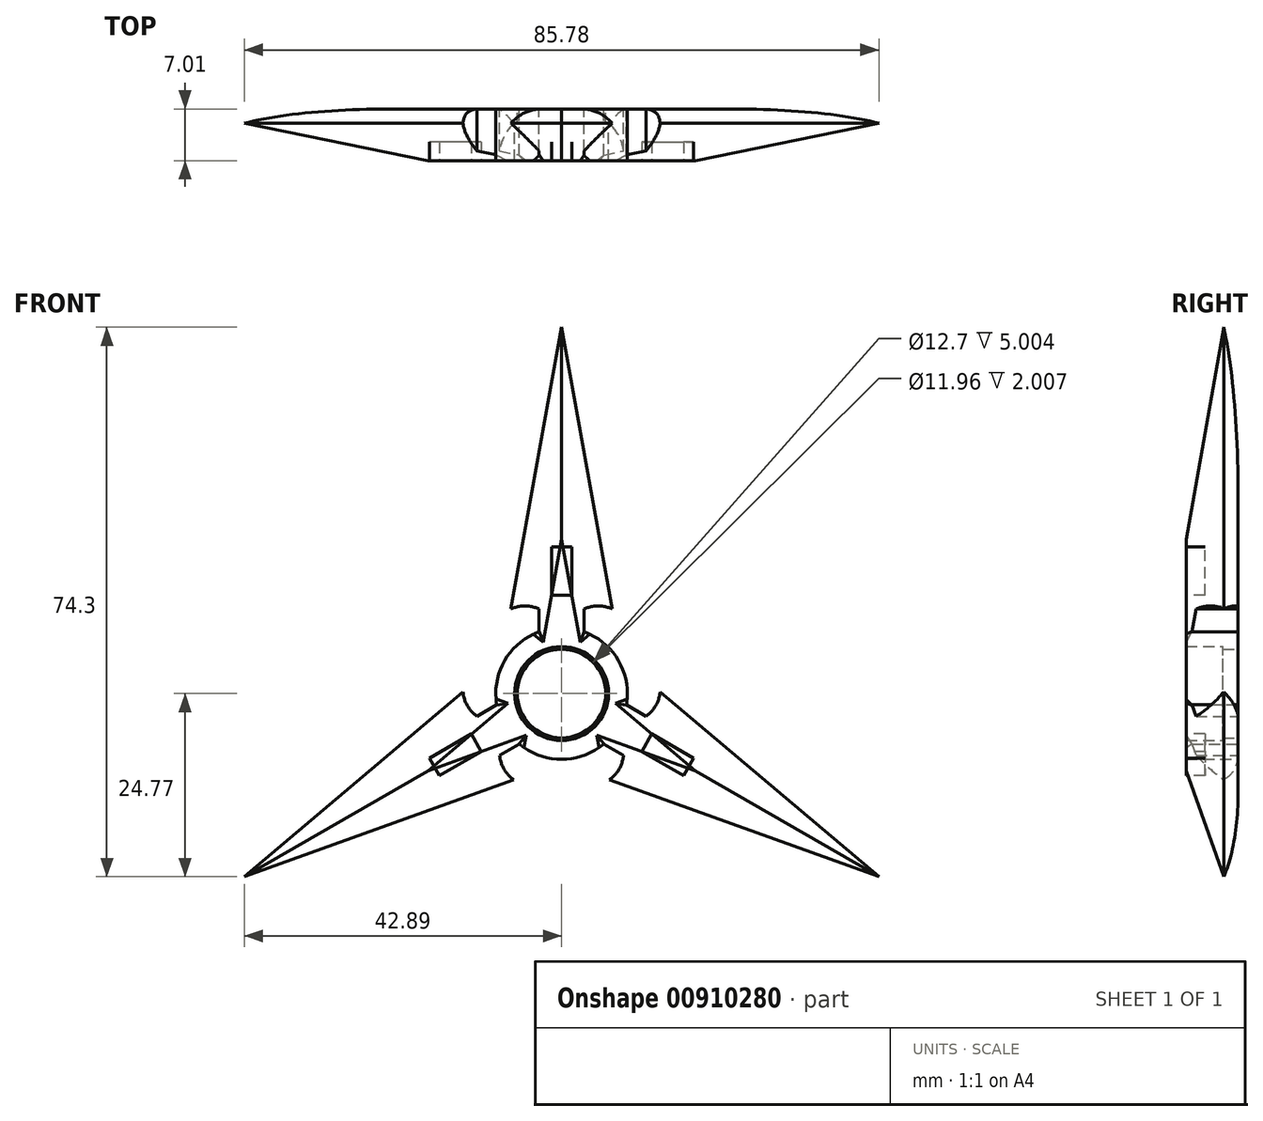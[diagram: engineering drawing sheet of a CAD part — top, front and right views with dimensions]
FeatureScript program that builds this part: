
annotation { "Feature Type Name" : "Feature", "Feature Type Description" : "" }
export const myFeature = defineFeature(function(context is Context, id is Id, definition is map)
    precondition{}
    {
        {
            var Q0;
            Q0=qCreatedBy(makeId("Front.planeOp"),FACE);
            var sketch = newSketch(context, id + "F0", { "sketchPlane" : qUnion([Q0])});
            skCircle(sketch, "E0", {"center": v(0, 0) * mm, "radius": 8.9 * mm});
            skCircle(sketch, "E1", {"center": v(0, 0) * mm, "radius": 6.35 * mm});
            skPoint(sketch, "E2", {"position": v(0, 8.9) * mm});
            skPoint(sketch, "E3", {"position": v(-3.05, 8.89) * mm});
            skPoint(sketch, "E4", {"position": v(3.05, 8.9) * mm});
            skLineSegment(sketch, "E5", {"start": v(-3.05, 8.89) * mm, "end": v(-3.05, 8.35) * mm});
            skLineSegment(sketch, "E6", {"start": v(3.05, 8.9) * mm, "end": v(3.05, 8.35) * mm});
            skLineSegment(sketch, "E7", {"start": v(3.05, 8.9) * mm, "end": v(3.05, 11.43) * mm});
            skLineSegment(sketch, "E8", {"start": v(-3.05, 8.89) * mm, "end": v(-3.05, 11.43) * mm});
            skPoint(sketch, "E9", {"position": v(-6.86, 11.43) * mm});
            skPoint(sketch, "E10", {"position": v(6.86, 11.43) * mm});
            skArc(sketch, "E11", {"start": v(-3.05, 11.43) * mm, "mid": v(-4.95, 11.84) * mm, "end": v(-6.86, 11.43) * mm});
            skArc(sketch, "E12", {"start": v(6.86, 11.43) * mm, "mid": v(4.95, 11.84) * mm, "end": v(3.05, 11.43) * mm});
            skPoint(sketch, "E13", {"position": v(6.86, 10.93) * mm});
            skPoint(sketch, "E14", {"position": v(-6.86, 10.75) * mm});
            skPoint(sketch, "E15", {"position": v(0, 49.53) * mm});
            skLineSegment(sketch, "E16", {"start": v(-6.86, 11.43) * mm, "end": v(0, 49.53) * mm});
            skLineSegment(sketch, "E17", {"start": v(0, 49.53) * mm, "end": v(6.86, 11.43) * mm});
            skSolve(sketch);
        }
        {
            var Q0;
            {var subQ1=sQuery(id+"F0.wireOp",EDGE,"E5");Q0=makeQuery(id+"F0.imprint","IMPRINT",FACE,{"disambiguationData":[TD([[makeQuery(id+"F0.imprint","IMPRINT",EDGE,{"derivedFrom":subQ1}),1.0]])]});}
            var Q1;
            Q1=makeQuery(id+"F0.imprint","IMPRINT",FACE,{"disambiguationData":[TD([[makeQuery(id+"F0.imprint","IMPRINT",EDGE,{"derivedFrom":sQuery(id+"F0.wireOp",EDGE,"E1")}),-1.0]])]});
            extrude(context, id + "F1", {"entities" : qUnion([Q0, Q1]), "depth" : 7 * mm, "offsetDistance" : 25.4 * mm});
        }
        {
            var Q0;
            Q0=makeQuery(id+"F1.opExtrude","CAP_EDGE",EDGE,{"disambiguationData":[OSD([sQuery(id+"F0.wireOp",EDGE,"E16")])],"isStart":false});
            var Q1;
            Q1=makeQuery(id+"F1.opExtrude","CAP_EDGE",EDGE,{"disambiguationData":[OSD([sQuery(id+"F0.wireOp",EDGE,"E17")])],"isStart":false});
            chamfer(context, id + "F2", {"entities" : qUnion([Q0, Q1]), "width" : 5.08 * mm, "tangentPropagation" : true});
        }
        {
            var Q0;
            Q0=makeQuery(id+"F1.opExtrude","CAP_EDGE",EDGE,{"disambiguationData":[OSD([sQuery(id+"F0.wireOp",EDGE,"E16")])],"isStart":true});
            var Q1;
            Q1=makeQuery(id+"F1.opExtrude","CAP_EDGE",EDGE,{"disambiguationData":[OSD([sQuery(id+"F0.wireOp",EDGE,"E17")])],"isStart":true});
            fillet(context, id + "F3", {"entities" : qUnion([Q0, Q1]), "radius" : 5.08 * mm, "tangentPropagation" : true, "allowEdgeOverflow" : false});
        }
        {
            var Q0;
            Q0=makeQuery(id+"F2.opChamfer","SPLIT",FACE,{"disambiguationData":[OD(1.0)],"derivedFrom":makeQuery(id+"F1.opExtrude","CAP_FACE",FACE,{"disambiguationData":[OSD([sQuery(id+"F0.wireOp",EDGE,"E0"),sQuery(id+"F0.wireOp",EDGE,"E1"),sQuery(id+"F0.wireOp",EDGE,"E5"),sQuery(id+"F0.wireOp",EDGE,"E6"),sQuery(id+"F0.wireOp",EDGE,"E7"),sQuery(id+"F0.wireOp",EDGE,"E8"),sQuery(id+"F0.wireOp",EDGE,"E11"),sQuery(id+"F0.wireOp",EDGE,"E12"),sQuery(id+"F0.wireOp",EDGE,"E16"),sQuery(id+"F0.wireOp",EDGE,"E17")])],"isStart":false})});
            var sketch = newSketch(context, id + "F4", { "sketchPlane" : qUnion([Q0])});
            skLineSegment(sketch, "E18.bottom", {"start": v(-1.36, 13.3) * mm, "end": v(1.36, 13.3) * mm});
            skLineSegment(sketch, "E18.top", {"start": v(-1.36, 19.84) * mm, "end": v(1.36, 19.84) * mm});
            skLineSegment(sketch, "E18.left", {"start": v(-1.36, 13.3) * mm, "end": v(-1.36, 19.84) * mm});
            skLineSegment(sketch, "E18.right", {"start": v(1.36, 13.3) * mm, "end": v(1.36, 19.84) * mm});
            skSolve(sketch);
        }
        {
            var Q0;
            {var subQ0=sQuery(id+"F4.wireOp",EDGE,"E18.bottom");Q0=makeQuery(id+"F4.imprint","IMPRINT",FACE,{"disambiguationData":[TD([[makeQuery(id+"F4.imprint","IMPRINT",EDGE,{"derivedFrom":subQ0}),1.0]])]});}
            var Q1;
            {var subQ0=sQuery(id+"F4.wireOp",EDGE,"E18.left");Q1=makeQuery(id+"F4.imprint","IMPRINT",FACE,{"disambiguationData":[TD([[makeQuery(id+"F4.imprint","IMPRINT",EDGE,{"derivedFrom":subQ0}),-1.0]])]});}
            var Q2;
            {var subQ0=sQuery(id+"F4.wireOp",EDGE,"E18.right");Q2=makeQuery(id+"F4.imprint","IMPRINT",FACE,{"disambiguationData":[TD([[makeQuery(id+"F4.imprint","IMPRINT",EDGE,{"derivedFrom":subQ0}),1.0]])]});}
            extrude(context, id + "F5", {"entities" : qUnion([Q0, Q1, Q2]), "oppositeDirection" : true, "depth" : 2.54 * mm, "offsetDistance" : 25.4 * mm});
        }
        {
            var Q0;
            Q0=makeQuery(id+"F5.opExtrude","SWEPT_BODY",BODY,{"disambiguationData":[OSD([sQuery(id+"F4.wireOp",EDGE,"E18.bottom"),sQuery(id+"F4.wireOp",EDGE,"E18.top"),sQuery(id+"F4.wireOp",EDGE,"E18.left"),sQuery(id+"F4.wireOp",EDGE,"E18.right")])]});
            var Q1;
            Q1=makeQuery(id+"F1.opExtrude","SWEPT_BODY",BODY,{"disambiguationData":[OSD([sQuery(id+"F0.wireOp",EDGE,"E0"),sQuery(id+"F0.wireOp",EDGE,"E1"),sQuery(id+"F0.wireOp",EDGE,"E5"),sQuery(id+"F0.wireOp",EDGE,"E6"),sQuery(id+"F0.wireOp",EDGE,"E7"),sQuery(id+"F0.wireOp",EDGE,"E8"),sQuery(id+"F0.wireOp",EDGE,"E11"),sQuery(id+"F0.wireOp",EDGE,"E12"),sQuery(id+"F0.wireOp",EDGE,"E16"),sQuery(id+"F0.wireOp",EDGE,"E17")])]});
            var Q2;
            Q2=makeQuery(id+"F1.opExtrude","SWEPT_FACE",FACE,{"disambiguationData":[OSD([sQuery(id+"F0.wireOp",EDGE,"E1")])]});
            circularPattern(context, id + "F6", {"entities" : qUnion([Q0, Q1]), "axis" : qUnion([Q2]), "angle" : 360 * degree, "instanceCount" : 3, "equalSpace" : true});
        }
        {
            var Q0;
            Q0=qCreatedBy(makeId("Front.planeOp"),FACE);
            var sketch = newSketch(context, id + "F7", { "sketchPlane" : qUnion([Q0])});
            skCircle(sketch, "E19", {"center": v(0, 0) * mm, "radius": 5.98 * mm});
            skCircle(sketch, "E20", {"center": v(0, 0) * mm, "radius": 6.35 * mm});
            skSolve(sketch);
        }
        {
            var Q0;
            Q0=makeQuery(id+"F7.imprint","IMPRINT",FACE,{"disambiguationData":[TD([[makeQuery(id+"F7.imprint","IMPRINT",EDGE,{"derivedFrom":sQuery(id+"F7.wireOp",EDGE,"E19")}),-1.0]])]});
            extrude(context, id + "F8", {"entities" : qUnion([Q0]), "operationType" : NewBodyOperationType.ADD, "depth" : 2 * mm, "offsetDistance" : 25.4 * mm});
        }
    });
